# Revit family: Lighting-Luminii-Clareo_Suspended
name_source: partatom
category: Lighting Fixtures
units: mm (PartAtom-declared; Revit-internal decimal feet)

## family parameters
Cut with Voids When Loaded = No
Host = Face
Light Source = Yes
OmniClass Number = 23.80.70.11.14.11
OmniClass Title = Downlights
Part Type = Normal
Room Calculation Point = No
Round Connector Dimension = Use Diameter
Shared = Yes

## types (2) — shared parameters
Apparent Load = 9 VA
Assembly Code = D5040.50
CCT = 3000K
Color Filter = 16777215
Constraints = 1
Control Type = Consult Manufacturer Website for more Information
Control Zone = Consult Manufacturer Website for more Information
Current Amps = 50 A
Default Elevation = 0"
Description = Linear Illumination System
Dimming Lamp Color Temperature Shift = <None>
Dimming Type = Consult Manufacturer Website for more Information
Emit from Line Length = 48"
Environment = Indoor
Finish = Metal - Luminii - Silver Anodized Aluminum
Frequency = 60 Hz
Has Battery Backup = No
Has Dimming = Yes
Height = 215/256"
Housing Protection Rating = Consult Manufacturer Website for more Information
Initial Color Comments = Perfomance based on 3000K Photometric Web File
Keynote = 26 50 00
Lamp = LED
Lamp Life = 1
Lens Material = Plastic - Luminii - Frosted Lens
Load Classification = Lighting
Luminaire Type = Linear Illumination System
Manufacturer = Luminii
Mounting Method = Mounting Options: Suspended
Number of Poles = 1
Operating Temperature = Consult Manufacturer Website for more Information
Phase = 1
Power Factor = 1
Power Source Type = Driver
Tilt Angle = -90.00°
URL = https://www.luminii.com
Version = 2020 - v1.0a
Voltage = 120 V
Voltage Comments = 120VAC - 277VAC
Warranty URL = https://www.luminii.com
Wattage Comments = 9.4 W/ft
Width = 197/256"

## per-type parameters (varying)
| type | Model | Photometric Web File | Product Page URL | S |
| Clareo Suspended - CLS | CLS | CLS-48-30K-LL60X2VHO-SF.IES | Consult Manufacturer Website for more Information | Yes |
| Clareo Suspended - CLQ | CLQ | CLS-48-30K-LL60X2VHO-RF.IES | https://www.luminii.com | No |

## geometry (parser evidence)
native form markers: Sweep x4
no freeform markers — native parametric forms only
